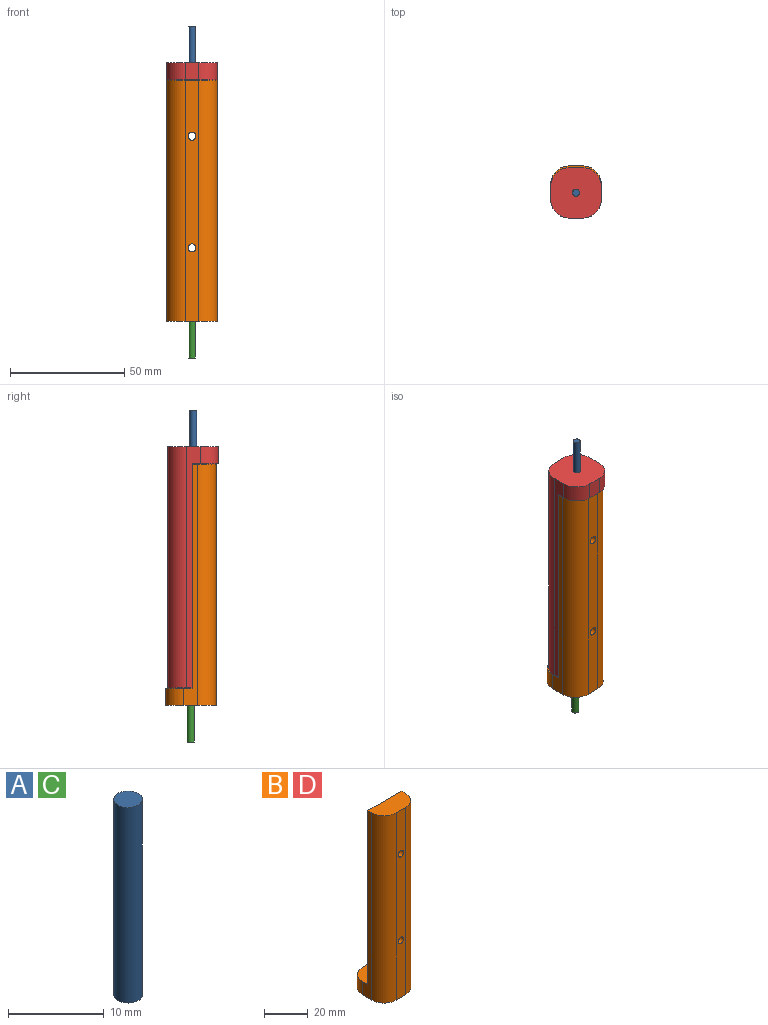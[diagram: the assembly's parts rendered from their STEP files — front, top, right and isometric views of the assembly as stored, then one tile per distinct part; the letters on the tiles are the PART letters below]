
ASSEMBLY  parts=4 mates=3
PART A: 3 faces, bbox 3x3x25 mm
  f0: cylinder r=1.5mm len=25mm, axis (0,0,-1), area 235.6mm2, adj f1,f2
  f1: plane 3x3mm, normal (0,0,1), area 7.1mm2, adj f0
  f2: plane 3x3mm, normal (0,0,-1), area 7.1mm2, adj f0
PART B: 22 faces, bbox 22x22x105.5 mm
  f0: plane 7.5x6mm, normal (0,1,0), area 45mm2, adj f5,f7,f10,f20
  f1: plane 105.5x6mm, normal (0,-1,0), area 613.8mm2, adj f5,f8,f9,f11,f12,f19
  f2: plane 105.5x6mm, normal (-1,0,0), area 290mm2, adj f5,f7,f8,f19,f20,f21
  f3: plane 105.5x6mm, normal (1,0,0), area 290mm2, adj f5,f9,f10,f19,f20,f21
  f4: cylinder r=1.6mm len=9mm, axis (0,0,-1), area 82.7mm2, adj f5,f6,f13,f14,f15,f16,f17,f18
  f5: plane 22x22mm, normal (0,0,-1), area 421mm2, adj f0,f1,f2,f3,f4,f7,f8,f9
  f6: plane 3.04x1.1mm, normal (0,0,-1), area 2.4mm2, adj f4,f21
  f7: cylinder r=8mm len=8mm, axis (0,0,-1), area 94.2mm2, adj f0,f2,f5,f20
  f8: cylinder r=8mm len=105.5mm, axis (0,0,1), area 1325.8mm2, adj f1,f2,f5,f19
  f9: cylinder r=8mm len=105.5mm, axis (0,0,-1), area 1325.8mm2, adj f1,f3,f5,f19
  f10: cylinder r=8mm len=8mm, axis (0,0,1), area 94.2mm2, adj f0,f3,f5,f20
  f11: cylinder r=1.75mm len=10.5mm, axis (0,1,0), area 115.5mm2, adj f1,f21
  f12: cylinder r=1.75mm len=10.5mm, axis (0,1,0), area 115.5mm2, adj f1,f21
  f13: plane 0.5x0.08mm, normal (0,0,1), area 0mm2, adj f4,f15,f21
  f14: plane 0.5x0.08mm, normal (0,0,1), area 0mm2, adj f4,f18,f21
  f15: plane 1.5x0.5mm, normal (-1,0,0), area 0.6mm2, adj f4,f13,f16,f21
  f16: plane 0.51x0.51mm, normal (0,0.71,-0.71), area 0mm2, adj f4,f15,f20
  f17: plane 0.51x0.51mm, normal (0,0.71,-0.71), area 0mm2, adj f4,f18,f20
  f18: plane 1.5x0.5mm, normal (1,0,0), area 0.6mm2, adj f4,f14,f17,f21
  f19: plane 22x10.5mm, normal (0,0,1), area 203.5mm2, adj f1,f2,f3,f8,f9,f21
  f20: plane 22x11.5mm, normal (0,0,1), area 219.9mm2, adj f0,f2,f3,f4,f7,f10,f16,f17
  f21: plane 98x22mm, normal (0,1,0), area 2132mm2, adj f2,f3,f6,f11,f12,f13,f14,f15
PART C: same geometry as A
PART D: same geometry as B
PLACE A rot(axis=(1,0,0),180deg) t=(25.07,-45.29,119.04)mm
PLACE B t=(-35.66,9.31,-10.15)mm fixed
PLACE C t=(25.07,62.92,-26.15)mm
PLACE D rot(axis=(1,0,0),180deg) t=(-35.66,8.31,103.04)mm
MATE fastened C.f0 <-> B.f4  axis (0,0,1) through (-35.66,9.31,-1.15)mm
MATE fastened B.f11 <-> D.f12  axis (0,1,0) through (-35.66,8.81,22.04)mm
MATE fastened A.f0 <-> D.f4  axis (0,0,-1) through (-35.66,8.31,94.04)mm
